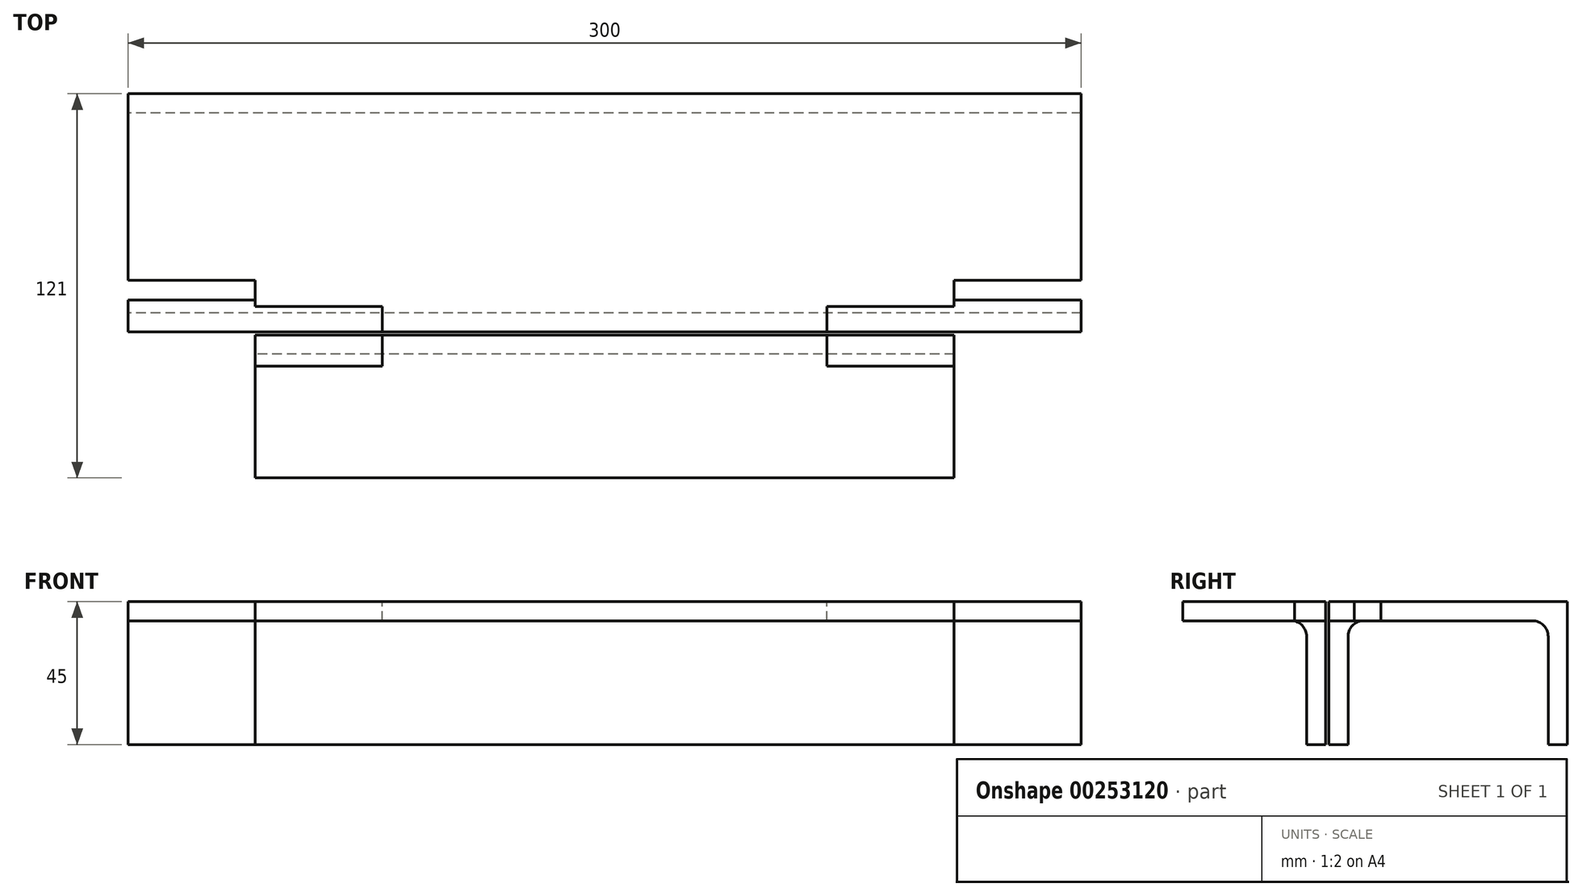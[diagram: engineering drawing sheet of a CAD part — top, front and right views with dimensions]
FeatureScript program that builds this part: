
annotation { "Feature Type Name" : "Feature", "Feature Type Description" : "" }
export const myFeature = defineFeature(function(context is Context, id is Id, definition is map)
    precondition{}
    {
        {
            var Q0;
            Q0=qCreatedBy(makeId("Top.planeOp"),FACE);
            var sketch = newSketch(context, id + "F0", { "sketchPlane" : qUnion([Q0])});
            skLineSegment(sketch, "E0", {"start": v(-150, 0) * mm, "end": v(150, 0) * mm});
            skPoint(sketch, "E1", {"position": v(0, 0) * mm});
            skSolve(sketch);
        }
        {
            var Q0;
            Q0=qCreatedBy(makeId("Right.planeOp"),FACE);
            var sketch = newSketch(context, id + "F1", { "sketchPlane" : qUnion([Q0])});
            skLineSegment(sketch, "E2", {"start": v(0, 0) * mm, "end": v(75, 0) * mm});
            skLineSegment(sketch, "E3", {"start": v(75, 0) * mm, "end": v(75, -45) * mm});
            skLineSegment(sketch, "E4", {"start": v(75, -45) * mm, "end": v(69, -45) * mm});
            skLineSegment(sketch, "E5", {"start": v(69, -45) * mm, "end": v(69, -11) * mm});
            skLineSegment(sketch, "E6", {"start": v(64, -6) * mm, "end": v(11, -6) * mm});
            skLineSegment(sketch, "E7", {"start": v(6, -11) * mm, "end": v(6, -45) * mm});
            skLineSegment(sketch, "E8", {"start": v(6, -45) * mm, "end": v(0, -45) * mm});
            skLineSegment(sketch, "E9", {"start": v(0, -45) * mm, "end": v(0, 0) * mm});
            skPoint(sketch, "E10.visualSharp", {"position": v(6, -6) * mm});
            skArc(sketch, "E10.filletArc", {"start": v(11, -6) * mm, "mid": v(7.46, -7.46) * mm, "end": v(6, -11) * mm});
            skPoint(sketch, "E11.visualSharp", {"position": v(69, -6) * mm});
            skArc(sketch, "E11.filletArc", {"start": v(69, -11) * mm, "mid": v(67.54, -7.46) * mm, "end": v(64, -6) * mm});
            skLineSegment(sketch, "E12", {"start": v(37.5, 0) * mm, "end": v(37.5, -6) * mm, "construction": true});
            skLineSegment(sketch, "E13", {"start": v(6, -28) * mm, "end": v(0, -28) * mm, "construction": true});
            skLineSegment(sketch, "E14", {"start": v(69, -28) * mm, "end": v(75, -28) * mm, "construction": true});
            skLineSegment(sketch, "E15", {"start": v(-46, 0) * mm, "end": v(-1, 0) * mm, "construction": true});
            skLineSegment(sketch, "E16", {"start": v(-1, 0) * mm, "end": v(-1, -45) * mm, "construction": true});
            skLineSegment(sketch, "E17", {"start": v(-1, -45) * mm, "end": v(-7, -45) * mm, "construction": true});
            skLineSegment(sketch, "E18", {"start": v(-7, -45) * mm, "end": v(-7, -11) * mm, "construction": true});
            skLineSegment(sketch, "E19", {"start": v(-12, -6) * mm, "end": v(-46, -6) * mm, "construction": true});
            skPoint(sketch, "E20.visualSharp", {"position": v(-7, -6) * mm});
            skArc(sketch, "E20.filletArc", {"start": v(-7, -11) * mm, "mid": v(-8.46, -7.46) * mm, "end": v(-12, -6) * mm, "construction": true});
            skLineSegment(sketch, "E21", {"start": v(-46, 0) * mm, "end": v(-46, -6) * mm, "construction": true});
            skLineSegment(sketch, "E22", {"start": v(0, 0) * mm, "end": v(-1, 0) * mm, "construction": true});
            skPoint(sketch, "E23", {"position": v(-0.5, 0) * mm});
            skCircle(sketch, "E24", {"center": v(-0.5, 0) * mm, "radius": 0.5 * mm, "construction": true});
            skCircle(sketch, "E25", {"center": v(-0.5, 0) * mm, "radius": 2.98 * mm, "construction": true});
            skSolve(sketch);
        }
        {
            var Q0;
            Q0 = qSketchRegion(id + "F1", true);
            var Q1;
            Q1=sQuery(id+"F0.wireOp",VERTEX,"E0.end");
            var Q2;
            Q2=sQuery(id+"F0.wireOp",VERTEX,"E0.start");
            extrude(context, id + "F2", {"entities" : qUnion([Q0]), "endBound" : BoundingType.UP_TO_VERTEX, "endBoundEntityVertex" : qUnion([Q1]), "depth" : 25 * mm, "hasSecondDirection" : true, "secondDirectionBound" : SecondDirectionBoundingType.UP_TO_VERTEX, "secondDirectionOppositeDirection" : true, "secondDirectionBoundEntityVertex" : qUnion([Q2]), "secondDirectionDepth" : 25 * mm});
        }
        {
            var Q0;
            Q0=qCreatedBy(makeId("Top.planeOp"),FACE);
            var sketch = newSketch(context, id + "F3", { "sketchPlane" : qUnion([Q0])});
            skLineSegment(sketch, "E26", {"start": v(110, -1) * mm, "end": v(-110, -1) * mm});
            skPoint(sketch, "E27", {"position": v(0, -1) * mm});
            skSolve(sketch);
        }
        {
            var Q0;
            Q0=qCreatedBy(makeId("Right.planeOp"),FACE);
            var sketch = newSketch(context, id + "F4", { "sketchPlane" : qUnion([Q0])});
            skLineSegment(sketch, "E28", {"start": v(-1, 0) * mm, "end": v(-46, 0) * mm});
            skLineSegment(sketch, "E29", {"start": v(-46, 0) * mm, "end": v(-46, -6) * mm});
            skLineSegment(sketch, "E30", {"start": v(-46, -6) * mm, "end": v(-12, -6) * mm});
            skLineSegment(sketch, "E31", {"start": v(-7, -11) * mm, "end": v(-7, -45) * mm});
            skLineSegment(sketch, "E32", {"start": v(-7, -45) * mm, "end": v(-1, -45) * mm});
            skLineSegment(sketch, "E33", {"start": v(-1, -45) * mm, "end": v(-1, 0) * mm});
            skPoint(sketch, "E34.visualSharp", {"position": v(-7, -6) * mm});
            skArc(sketch, "E34.filletArc", {"start": v(-7, -11) * mm, "mid": v(-8.46, -7.46) * mm, "end": v(-12, -6) * mm});
            skSolve(sketch);
        }
        {
            var Q0;
            Q0 = qSketchRegion(id + "F4", true);
            var Q1;
            Q1=sQuery(id+"F3.wireOp",VERTEX,"E26.start");
            var Q2;
            Q2=sQuery(id+"F3.wireOp",VERTEX,"E26.end");
            extrude(context, id + "F5", {"entities" : qUnion([Q0]), "endBound" : BoundingType.UP_TO_VERTEX, "endBoundEntityVertex" : qUnion([Q1]), "depth" : 25 * mm, "hasSecondDirection" : true, "secondDirectionBound" : SecondDirectionBoundingType.UP_TO_VERTEX, "secondDirectionOppositeDirection" : true, "secondDirectionBoundEntityVertex" : qUnion([Q2]), "secondDirectionDepth" : 25 * mm});
        }
        {
            var Q0;
            Q0=makeQuery(id+"F2.opExtrude","SWEPT_FACE",FACE,{"disambiguationData":[OSD([sQuery(id+"F1.wireOp",EDGE,"E2")])]});
            var sketch = newSketch(context, id + "F6", { "sketchPlane" : qUnion([Q0])});
            skLineSegment(sketch, "E35", {"start": v(0, 75) * mm, "end": v(0, 0) * mm, "construction": true});
            skLineSegment(sketch, "E36.bottom", {"start": v(-150, 0) * mm, "end": v(-110, 0) * mm});
            skLineSegment(sketch, "E36.top", {"start": v(-150, 16.3) * mm, "end": v(-110, 16.3) * mm});
            skLineSegment(sketch, "E36.left", {"start": v(-150, 0) * mm, "end": v(-150, 16.3) * mm});
            skLineSegment(sketch, "E36.right", {"start": v(-110, 8) * mm, "end": v(-110, 16.3) * mm});
            skLineSegment(sketch, "E37.bottom", {"start": v(-110, 0) * mm, "end": v(-70, 0) * mm});
            skLineSegment(sketch, "E37.top", {"start": v(-110, 8) * mm, "end": v(-70, 8) * mm});
            skLineSegment(sketch, "E37.right", {"start": v(-70, 0) * mm, "end": v(-70, 8) * mm});
            skLineSegment(sketch, "E38.MirrorCS", {"start": v(150, 0) * mm, "end": v(110, 0) * mm});
            skLineSegment(sketch, "E39.MirrorCS", {"start": v(70, 0) * mm, "end": v(70, 8) * mm});
            skLineSegment(sketch, "E40.MirrorCS", {"start": v(150, 0) * mm, "end": v(150, 16.3) * mm});
            skLineSegment(sketch, "E41.MirrorCS", {"start": v(110, 8) * mm, "end": v(70, 8) * mm});
            skLineSegment(sketch, "E42.MirrorCS", {"start": v(110, 8) * mm, "end": v(110, 16.3) * mm});
            skLineSegment(sketch, "E43.MirrorCS", {"start": v(150, 16.3) * mm, "end": v(110, 16.3) * mm});
            skLineSegment(sketch, "E44.MirrorCS", {"start": v(110, 0) * mm, "end": v(70, 0) * mm});
            skSolve(sketch);
        }
        {
            var Q0;
            Q0 = qSketchRegion(id + "F6", true);
            extrude(context, id + "F7", {"entities" : qUnion([Q0]), "operationType" : NewBodyOperationType.REMOVE, "oppositeDirection" : true, "depth" : 6.1 * mm});
        }
        {
            var Q0;
            Q0=makeQuery(id+"F5.opExtrude","SWEPT_FACE",FACE,{"disambiguationData":[OSD([sQuery(id+"F4.wireOp",EDGE,"E28")])]});
            var sketch = newSketch(context, id + "F8", { "sketchPlane" : qUnion([Q0])});
            skLineSegment(sketch, "E45.bottom", {"start": v(-110, -1) * mm, "end": v(-70, -1) * mm});
            skLineSegment(sketch, "E45.top", {"start": v(-110, -10.8) * mm, "end": v(-70, -10.8) * mm});
            skLineSegment(sketch, "E45.left", {"start": v(-110, -1) * mm, "end": v(-110, -10.8) * mm});
            skLineSegment(sketch, "E45.right", {"start": v(-70, -1) * mm, "end": v(-70, -10.8) * mm});
            skLineSegment(sketch, "E46", {"start": v(0, -1) * mm, "end": v(0, -46) * mm, "construction": true});
            skLineSegment(sketch, "E47.MirrorCS", {"start": v(70, -1) * mm, "end": v(70, -10.8) * mm});
            skLineSegment(sketch, "E48.MirrorCS", {"start": v(110, -1) * mm, "end": v(110, -10.8) * mm});
            skLineSegment(sketch, "E49.MirrorCS", {"start": v(110, -1) * mm, "end": v(70, -1) * mm});
            skLineSegment(sketch, "E50.MirrorCS", {"start": v(110, -10.8) * mm, "end": v(70, -10.8) * mm});
            skSolve(sketch);
        }
        {
            var Q0;
            Q0 = qSketchRegion(id + "F8", true);
            extrude(context, id + "F9", {"entities" : qUnion([Q0]), "operationType" : NewBodyOperationType.REMOVE, "oppositeDirection" : true, "depth" : 6 * mm});
        }
    });
